# Revit family: 700_OXXO_Standard
name_source: partatom
category: Doors
revit_build: Autodesk Revit 2014 (Build: 20130308_1515(x64)
units: mm (PartAtom-declared; Revit-internal decimal feet)

## types (16) — shared parameters
Centered In Wall = Yes
Custom Door Height = 2090 mm  [stored 6.85696 ft]
Custom Sash Width Side = 800 mm
Description = Sliding door, OXXO
Equal Sash Width = Yes
Frame Thickness = 72 mm
Height = 2090 mm  [stored 6.85696 ft]
Limit Door Height Max = 2142 mm
Limit Door Height Min = 342 mm
Limit Door Width Min = 1183 mm
Limit Sash Height Max = 2100 mm
Limit Sash Height Min = 300 mm  [stored 0.984252 ft]
Limit Sash Width Max = 1500 mm
Limit Sash Width Min = 300 mm  [stored 0.984252 ft]
Manufacturer = Crealco
Model = Series 700
Sash Frame Seal = 2 mm  [stored 0.00656168 ft]
Sash Frame Side Gap = 10 mm  [stored 0.0328084 ft]
Sash Frame Top Gap = 16 mm  [stored 0.0524934 ft]
Sash Height = 2048 mm
Sash Sliding Frame Seal = 5 mm  [stored 0.0164042 ft]
URL = http://www.crealco.co.za
Wall Closure = By host
zero-valued in all types: Custom Frame Offset From Exterior, Default Sill Height

## per-type parameters (varying)
| type | Area Middle Sash Glazing | Area Side Sash Glazing | Custom Door Width | Custom Windload | Interlock Configuration | Intruderprufe LowE SHGC Value | Intruderprufe LowE U Value | Intruderprufe SHGC Value | Limit Door Width Max | Limit Sash Width Side Max | Limit Sash Width Side Min | Max Pane Area | Meeting Stile Configuration | Sash Width Middle | Sash Width Sides | Toughened Safety SHGC Value | Toughened Safety U Value | Width | Windload Design |
| 700-3021OXXO-1000Pa | 1.34 m² | 1.38 m² | 2990 mm | 1000 mm  [stored 3.28084 ft] | 2 mm  [stored 0.00656168 ft] | 0.611 | 4.55 | 0.693 | 5983 mm  [stored 19.6293 ft] | 1204 mm | 300 mm  [stored 0.984252 ft] | 1.38 m² | 1 mm  [stored 0.00328084 ft] | 752 mm | 752 mm | 0.731 | 6.1 | 2990 mm | 1000 mm  [stored 3.28084 ft] |
| 700-3021OXXO-1500Pa | 1.34 m² | 1.38 m² | 2990 mm | 1500 mm | 3 mm  [stored 0.00984252 ft] | 0.611 | 4.55 | 0.693 | 5983 mm  [stored 19.6293 ft] | 1204 mm | 300 mm  [stored 0.984252 ft] | 1.38 m² | 2 mm  [stored 0.00656168 ft] | 752 mm | 752 mm | 0.731 | 6.1 | 2990 mm | 1500 mm |
| 700-3021OXXO-2000Pa | 1.34 m² | 1.38 m² | 2990 mm | 2000 mm  [stored 6.56168 ft] | 3 mm  [stored 0.00984252 ft] | 0.611 | 4.55 | 0.693 | 3590 mm | 1204 mm | 300 mm  [stored 0.984252 ft] | 1.38 m² | 2 mm  [stored 0.00656168 ft] | 752 mm | 752 mm | 0.731 | 6.1 | 2990 mm | 2000 mm  [stored 6.56168 ft] |
| 700-3621OXXO-1000Pa | 1.63 m² | 1.67 m² | 3590 mm | 1000 mm  [stored 3.28084 ft] | 2 mm  [stored 0.00656168 ft] | 0.619 | 4.46 | 0.702 | 5983 mm  [stored 19.6293 ft] | 1500 mm | 304 mm | 1.67 m² | 1 mm  [stored 0.00328084 ft] | 902 mm | 902 mm | 0.74 | 6.08 | 3590 mm | 1000 mm  [stored 3.28084 ft] |
| 700-3621OXXO-1500Pa | 1.63 m² | 1.67 m² | 3590 mm | 1500 mm | 3 mm  [stored 0.00984252 ft] | 0.619 | 4.46 | 0.702 | 5983 mm  [stored 19.6293 ft] | 1500 mm | 304 mm | 1.67 m² | 2 mm  [stored 0.00656168 ft] | 902 mm | 902 mm | 0.74 | 6.08 | 3590 mm | 1500 mm |
| 700-3621OXXO-2000Pa | 1.63 m² | 1.67 m² | 3590 mm | 2000 mm  [stored 6.56168 ft] | 3 mm  [stored 0.00984252 ft] | 0.619 | 4.46 | 0.702 | 3590 mm | 1500 mm | 304 mm | 1.67 m² | 2 mm  [stored 0.00656168 ft] | 902 mm | 902 mm | 0.74 | 6.08 | 3590 mm | 2000 mm  [stored 6.56168 ft] |
| 700-4021OXXO-1000Pa | 1.83 m² | 1.87 m² | 3990 mm  [stored 13.0906 ft] | 1000 mm  [stored 3.28084 ft] | 2 mm  [stored 0.00656168 ft] | 0.633 | 4.29 | 0.718 | 5983 mm  [stored 19.6293 ft] | 1500 mm | 504 mm | 1.87 m² | 1 mm  [stored 0.00328084 ft] | 1002 mm | 1002 mm | 0.758 | 6.03 | 3990 mm  [stored 13.0906 ft] | 1000 mm  [stored 3.28084 ft] |
| 700-4021OXXO-1500Pa | 1.83 m² | 1.87 m² | 3990 mm  [stored 13.0906 ft] | 1500 mm | 3 mm  [stored 0.00984252 ft] | 0.622 | 4.42 | 0.706 | 5983 mm  [stored 19.6293 ft] | 1500 mm | 504 mm | 1.87 m² | 2 mm  [stored 0.00656168 ft] | 1002 mm | 1002 mm | 0.744 | 6.07 | 3990 mm  [stored 13.0906 ft] | 1500 mm |
| 700-4221OXXO-1000Pa | 1.93 m² | 1.97 m² | 4190 mm  [stored 13.7467 ft] | 1000 mm  [stored 3.28084 ft] | 3 mm  [stored 0.00984252 ft] | 0.624 | 4.4 | 0.708 | 5983 mm  [stored 19.6293 ft] | 1500 mm | 604 mm | 1.97 m² | 1 mm  [stored 0.00328084 ft] | 1052 mm | 1052 mm | 0.746 | 6.06 | 4190 mm  [stored 13.7467 ft] | 1000 mm  [stored 3.28084 ft] |
| 700-4221OXXO-1500Pa | 1.93 m² | 1.97 m² | 4190 mm  [stored 13.7467 ft] | 1500 mm | 3 mm  [stored 0.00984252 ft] | 0.624 | 4.4 | 0.708 | 5983 mm  [stored 19.6293 ft] | 1500 mm | 604 mm | 1.97 m² | 2 mm  [stored 0.00656168 ft] | 1052 mm | 1052 mm | 0.746 | 6.06 | 4190 mm  [stored 13.7467 ft] | 1500 mm |
| 700-4821OXXO-1000Pa | 2.22 m² | 2.26 m² | 4790 mm | 1000 mm  [stored 3.28084 ft] | 3 mm  [stored 0.00984252 ft] | 0.628 | 4.36 | 0.712 | 5983 mm  [stored 19.6293 ft] | 1500 mm | 904 mm | 2.26 m² | 2 mm  [stored 0.00656168 ft] | 1202 mm | 1202 mm | 0.751 | 6.05 | 4790 mm | 1000 mm  [stored 3.28084 ft] |
| 700-4821OXXO-1500Pa | 2.22 m² | 2.26 m² | 4790 mm | 1500 mm | 3 mm  [stored 0.00984252 ft] | 0.628 | 4.36 | 0.712 | 5983 mm  [stored 19.6293 ft] | 1500 mm | 904 mm | 2.26 m² | 2 mm  [stored 0.00656168 ft] | 1202 mm | 1202 mm | 0.751 | 6.05 | 4790 mm | 1500 mm |
| 700-5421OXXO-1000Pa | 2.52 m² | 2.56 m² | 5390 mm | 1000 mm  [stored 3.28084 ft] | 3 mm  [stored 0.00984252 ft] | 0.631 | 4.32 | 0.716 | 5983 mm  [stored 19.6293 ft] | 1500 mm | 1204 mm | 2.56 m² | 2 mm  [stored 0.00656168 ft] | 1352 mm | 1352 mm | 0.755 | 6.04 | 5390 mm | 1000 mm  [stored 3.28084 ft] |
| 700-5421OXXO-1500Pa | 2.52 m² | 2.56 m² | 5390 mm | 1500 mm | 3 mm  [stored 0.00984252 ft] | 0.631 | 4.32 | 0.716 | 5983 mm  [stored 19.6293 ft] | 1500 mm | 1204 mm | 2.56 m² | 2 mm  [stored 0.00656168 ft] | 1352 mm | 1352 mm | 0.755 | 6.04 | 5390 mm | 1500 mm |
| 700-6021OXXO-1000Pa | 2.81 m² | 2.85 m² | 5990 mm | 1000 mm  [stored 3.28084 ft] | 3 mm  [stored 0.00984252 ft] | 0.633 | 4.29 | 0.718 | 5983 mm  [stored 19.6293 ft] | 1500 mm | 1500 mm | 2.85 m² | 2 mm  [stored 0.00656168 ft] | 1500 mm | 1500 mm | 0.758 | 6.03 | 5983 mm  [stored 19.6293 ft] | 1000 mm  [stored 3.28084 ft] |
| 700-6021OXXO-1500Pa | 2.81 m² | 2.85 m² | 5990 mm | 1500 mm | 3 mm  [stored 0.00984252 ft] | 0.633 | 4.29 | 0.718 | 5983 mm  [stored 19.6293 ft] | 1500 mm | 1500 mm | 2.85 m² | 2 mm  [stored 0.00656168 ft] | 1500 mm | 1500 mm | 0.758 | 6.03 | 5983 mm  [stored 19.6293 ft] | 1500 mm |

note: [stored X ft] marks values corroborated as IEEE doubles in the binary element streams (Revit-internal decimal feet)

## geometry (parser evidence)
native form markers: Sweep x75
no freeform markers — native parametric forms only
